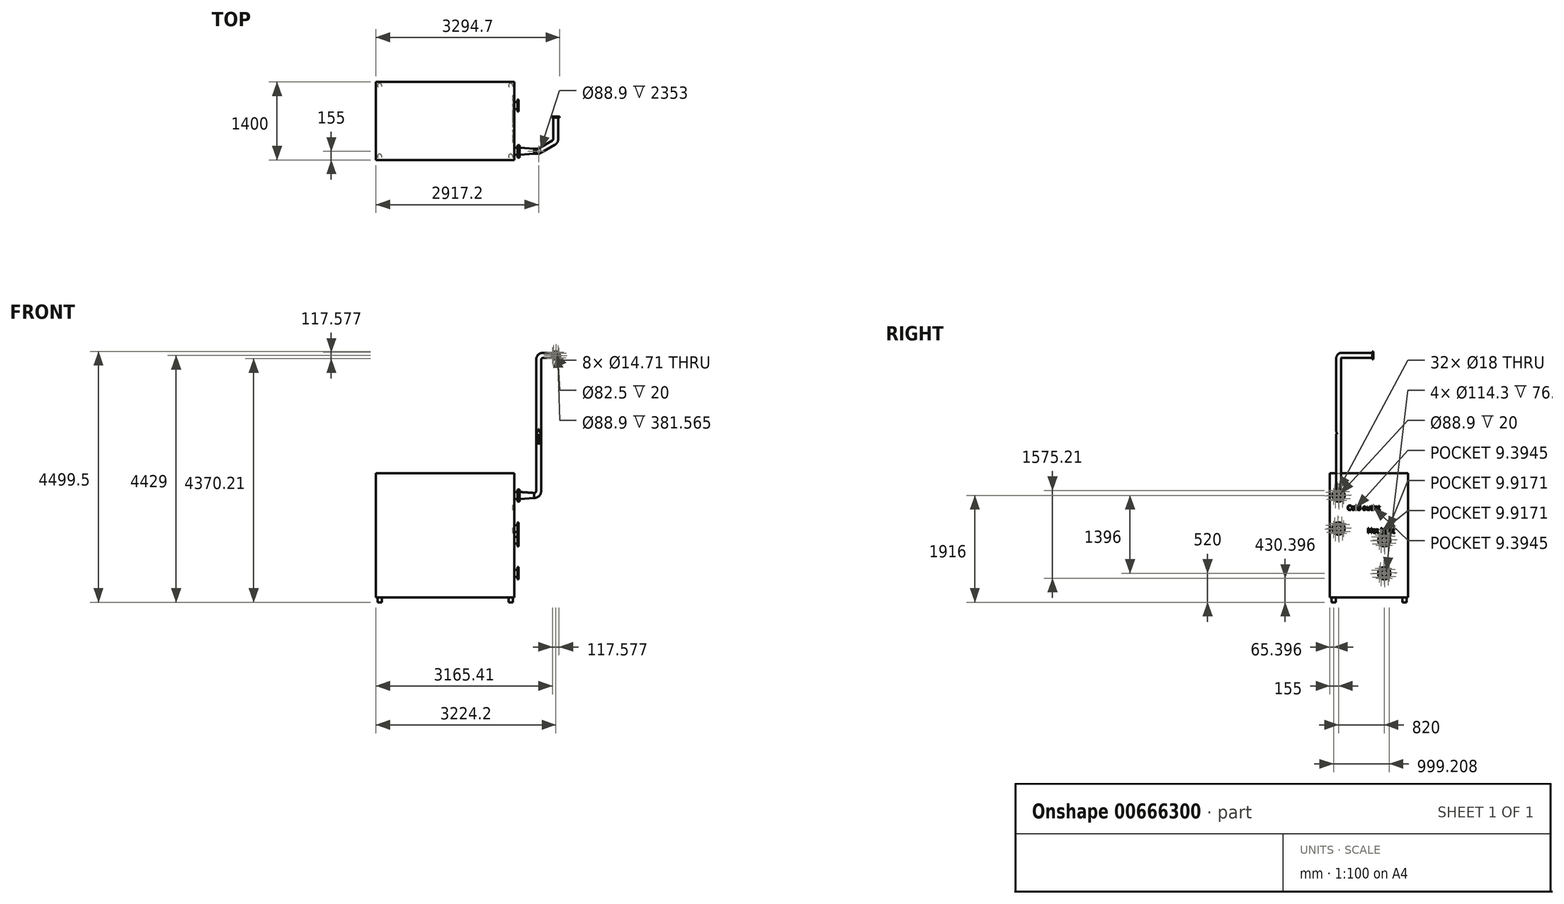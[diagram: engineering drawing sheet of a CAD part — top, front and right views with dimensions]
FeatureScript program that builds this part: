
annotation { "Feature Type Name" : "Feature", "Feature Type Description" : "" }
export const myFeature = defineFeature(function(context is Context, id is Id, definition is map)
    precondition{}
    {
        {
            var Q0;
            Q0=qCreatedBy(makeId("Top.planeOp"),FACE);
            var sketch = newSketch(context, id + "F0", { "sketchPlane" : qUnion([Q0])});
            skLineSegment(sketch, "E0.bottom", {"start": v(0, 0) * mm, "end": v(2481, 0) * mm});
            skLineSegment(sketch, "E0.top", {"start": v(0, 1400) * mm, "end": v(2481, 1400) * mm});
            skLineSegment(sketch, "E0.left", {"start": v(0, 0) * mm, "end": v(0, 1400) * mm});
            skLineSegment(sketch, "E0.right", {"start": v(2481, 0) * mm, "end": v(2481, 1400) * mm});
            skSolve(sketch);
        }
        {
            var Q0;
            Q0=qSketchRegion(id+"F0",true);
            extrude(context, id + "F1", {"entities" : qUnion([Q0]), "depth" : (2228 + 90) * mm});
        }
        {
            var Q0;
            Q0=makeQuery(id+"F1.opExtrude","SWEPT_FACE",FACE,{"disambiguationData":[OSD([sQuery(id+"F0.wireOp",EDGE,"E0.right")])]});
            var sketch = newSketch(context, id + "F2", { "sketchPlane" : qUnion([Q0])});
            skCircle(sketch, "E1", {"center": v(155, 1916) * mm, "radius": 57.15 * mm});
            skCircle(sketch, "E2", {"center": v(155, 1916) * mm, "radius": 62.15 * mm});
            skCircle(sketch, "E3", {"center": v(155, 1916) * mm, "radius": 110 * mm});
            skCircle(sketch, "E4", {"center": v(155, 1916) * mm, "radius": 90 * mm, "construction": true});
            skCircle(sketch, "E5", {"center": v(163.43, 1826.4) * mm, "radius": 9 * mm});
            skCircle(sketch, "E6.1.0", {"center": v(224.32, 1858.6) * mm, "radius": 9 * mm});
            skCircle(sketch, "E6.2.0", {"center": v(244.6, 1924.43) * mm, "radius": 9 * mm});
            skCircle(sketch, "E6.3.0", {"center": v(212.4, 1985.32) * mm, "radius": 9 * mm});
            skCircle(sketch, "E6.4.0", {"center": v(146.57, 2005.6) * mm, "radius": 9 * mm});
            skCircle(sketch, "E6.5.0", {"center": v(85.68, 1973.4) * mm, "radius": 9 * mm});
            skCircle(sketch, "E6.6.0", {"center": v(65.4, 1907.57) * mm, "radius": 9 * mm});
            skCircle(sketch, "E6.7.0", {"center": v(97.6, 1846.68) * mm, "radius": 9 * mm});
            skPoint(sketch, "E7.0.1.2", {"position": v(155, 1323) * mm});
            skCircle(sketch, "E7.0.1.4", {"center": v(155, 1323) * mm, "radius": 57.15 * mm});
            skCircle(sketch, "E7.0.1.5", {"center": v(155, 1323) * mm, "radius": 62.15 * mm});
            skCircle(sketch, "E7.0.1.6", {"center": v(155, 1323) * mm, "radius": 110 * mm});
            skCircle(sketch, "E7.0.1.7", {"center": v(155, 1323) * mm, "radius": 90 * mm, "construction": true});
            skCircle(sketch, "E7.0.1.13", {"center": v(97.6, 1253.68) * mm, "radius": 9 * mm});
            skCircle(sketch, "E7.0.1.15", {"center": v(244.6, 1331.43) * mm, "radius": 9 * mm});
            skCircle(sketch, "E7.0.1.16", {"center": v(212.4, 1392.32) * mm, "radius": 9 * mm});
            skCircle(sketch, "E7.0.1.17", {"center": v(146.57, 1412.6) * mm, "radius": 9 * mm});
            skCircle(sketch, "E7.0.1.18", {"center": v(163.43, 1233.4) * mm, "radius": 9 * mm});
            skCircle(sketch, "E7.0.1.19", {"center": v(85.68, 1380.4) * mm, "radius": 9 * mm});
            skCircle(sketch, "E7.0.1.20", {"center": v(65.4, 1314.57) * mm, "radius": 9 * mm});
            skCircle(sketch, "E7.0.1.21", {"center": v(224.32, 1265.6) * mm, "radius": 9 * mm});
            skLineSegment(sketch, "E7.direction1", {"start": v(97.6, 1846.68) * mm, "end": v(122.6, 1846.68) * mm, "construction": true});
            skLineSegment(sketch, "E7.direction2", {"start": v(97.6, 1846.68) * mm, "end": v(97.6, 1259.36) * mm, "construction": true});
            skSolve(sketch);
        }
        {
            var Q0;
            Q0=makeQuery(id+"F2.imprint","IMPRINT",FACE,{"disambiguationData":[TD([[makeQuery(id+"F2.imprint","IMPRINT",EDGE,{"derivedFrom":sQuery(id+"F2.wireOp",EDGE,"E1")}),-1.0]])]});
            var Q1;
            Q1=makeQuery(id+"F2.imprint","IMPRINT",FACE,{"disambiguationData":[TD([[makeQuery(id+"F2.imprint","IMPRINT",EDGE,{"derivedFrom":sQuery(id+"F2.wireOp",EDGE,"E7.0.1.4")}),-1.0]])]});
            extrude(context, id + "F3", {"entities" : qUnion([Q0, Q1]), "depth" : (76.2 - 22) * mm});
        }
        {
            var Q0;
            Q0=makeQuery(id+"F2.imprint","IMPRINT",FACE,{"disambiguationData":[TD([[makeQuery(id+"F2.imprint","IMPRINT",EDGE,{"derivedFrom":sQuery(id+"F2.wireOp",EDGE,"E7.0.1.4")}),-1.0]])]});
            var Q1;
            Q1=makeQuery(id+"F2.imprint","IMPRINT",FACE,{"disambiguationData":[TD([[makeQuery(id+"F2.imprint","IMPRINT",EDGE,{"derivedFrom":sQuery(id+"F2.wireOp",EDGE,"E7.0.1.5")}),-1.0]])]});
            var Q2;
            Q2=makeQuery(id+"F2.imprint","IMPRINT",FACE,{"disambiguationData":[TD([[makeQuery(id+"F2.imprint","IMPRINT",EDGE,{"derivedFrom":sQuery(id+"F2.wireOp",EDGE,"E1")}),-1.0]])]});
            var Q3;
            Q3=makeQuery(id+"F2.imprint","IMPRINT",FACE,{"disambiguationData":[TD([[makeQuery(id+"F2.imprint","IMPRINT",EDGE,{"derivedFrom":sQuery(id+"F2.wireOp",EDGE,"E2")}),-1.0]])]});
            var Q4;
            Q4=makeQuery(id+"F3.opExtrude","CAP_FACE",FACE,{"disambiguationData":[OSD([sQuery(id+"F2.wireOp",EDGE,"E7.0.1.4"),sQuery(id+"F2.wireOp",EDGE,"E7.0.1.5")])],"isStart":false});
            extrude(context, id + "F4", {"entities" : qUnion([Q0, Q1, Q2, Q3]), "operationType" : NewBodyOperationType.ADD, "depth" : 76.2 * mm, "hasSecondDirection" : true, "secondDirectionBound" : BoundingType.UP_TO_SURFACE, "secondDirectionOppositeDirection" : false, "secondDirectionBoundEntityFace" : qUnion([Q4]), "secondDirectionDepth" : 104.68 * mm});
        }
        {
            var Q0;
            Q0=makeQuery(id+"F3.opExtrude","SWEPT_BODY",BODY,{"disambiguationData":[OSD([sQuery(id+"F2.wireOp",EDGE,"E1"),sQuery(id+"F2.wireOp",EDGE,"E2")])]});
            var Q1;
            Q1=makeQuery(id+"F3.opExtrude","SWEPT_BODY",BODY,{"disambiguationData":[OSD([sQuery(id+"F2.wireOp",EDGE,"E7.0.1.4"),sQuery(id+"F2.wireOp",EDGE,"E7.0.1.5")])]});
            transform(context, id + "F5", {"entities" : qUnion([Q0, Q1]), "transformType" : TransformType.TRANSLATION_3D, "dx" : 0 * mm, "dy" : (975 - 155) * mm, "dz" : (430 - 1233) * mm, "makeCopy" : true});
        }
        {
            var Q0;
            Q0=makeQuery(id+"F1.opExtrude","SWEPT_BODY",BODY,{"disambiguationData":[OSD([sQuery(id+"F0.wireOp",EDGE,"E0.bottom"),sQuery(id+"F0.wireOp",EDGE,"E0.top"),sQuery(id+"F0.wireOp",EDGE,"E0.left"),sQuery(id+"F0.wireOp",EDGE,"E0.right")])]});
            var Q1;
            Q1=makeQuery(id+"F3.opExtrude","SWEPT_BODY",BODY,{"disambiguationData":[OSD([sQuery(id+"F2.wireOp",EDGE,"E1"),sQuery(id+"F2.wireOp",EDGE,"E2")])]});
            var Q2;
            Q2=makeQuery(id+"F3.opExtrude","SWEPT_BODY",BODY,{"disambiguationData":[OSD([sQuery(id+"F2.wireOp",EDGE,"E7.0.1.4"),sQuery(id+"F2.wireOp",EDGE,"E7.0.1.5")])]});
            var Q3;
            Q3=makeQuery(id+"F5.opPattern","COPY",BODY,{"derivedFrom":makeQuery(id+"F3.opExtrude","SWEPT_BODY",BODY,{"disambiguationData":[OSD([sQuery(id+"F2.wireOp",EDGE,"E7.0.1.4"),sQuery(id+"F2.wireOp",EDGE,"E7.0.1.5")])]}),"instanceName":"1"});
            var Q4;
            Q4=makeQuery(id+"F5.opPattern","COPY",BODY,{"derivedFrom":makeQuery(id+"F3.opExtrude","SWEPT_BODY",BODY,{"disambiguationData":[OSD([sQuery(id+"F2.wireOp",EDGE,"E1"),sQuery(id+"F2.wireOp",EDGE,"E2")])]}),"instanceName":"1"});
            booleanBodies(context, id + "F6", {"operationType" : BooleanOperationType.UNION, "tools" : qUnion([Q0, Q1, Q2, Q3, Q4])});
        }
        {
            var Q0;
            Q0=makeQuery(id+"F2.imprint","IMPRINT",FACE,{"disambiguationData":[TD([[makeQuery(id+"F2.imprint","IMPRINT",EDGE,{"derivedFrom":sQuery(id+"F2.wireOp",EDGE,"E3")}),-1.0]])]});
            var sketch = newSketch(context, id + "F7", { "sketchPlane" : qUnion([Q0])});
            skText(sketch, "E8", { "text": "Hot inlet", "fontName": "OpenSans-Regular.ttf"});
            skText(sketch, "E9", { "text": "Cold outlet\n", "fontName": "OpenSans-Regular.ttf"});
            const initialGuessF7  = {"E8": [0.67256, 1.24268, 1, 0, 0.08805], "E9": [0.3111, 1.65511, 1, 0, 0.08341]};
            skSetInitialGuess(sketch, initialGuessF7);
            skSolve(sketch);
        }
        {
            var Q0;
            Q0=qSketchRegion(id+"F7",true);
            extrude(context, id + "F8", {"entities" : qUnion([Q0]), "operationType" : NewBodyOperationType.REMOVE, "oppositeDirection" : true, "depth" : 25 * mm});
        }
        {
            var Q0;
            Q0=sQuery(id+"F2.wireOp",VERTEX,"E1.center");
            var Q1;
            Q1=qCreatedBy(makeId("Front.planeOp"),FACE);
            cPlane(context, id + "F9", {"entities" : qUnion([Q0, Q1]), "cplaneType" : CPlaneType.PLANE_POINT, "offset" : 150 * mm, "width" : 150 * mm, "height" : 150 * mm});
        }
        {
            var Q0;
            Q0=qCreatedBy(id+"F9.planeOp",FACE);
            var sketch = newSketch(context, id + "F10", { "sketchPlane" : qUnion([Q0])});
            skLineSegment(sketch, "E10.0", {"start": v(2557.2, 1973.15) * mm, "end": v(2557.2, 1858.85) * mm});
            skPoint(sketch, "E11", {"position": v(2557.2, 1916) * mm});
            skLineSegment(sketch, "E12", {"start": v(2557.2, 1916) * mm, "end": v(2837.2, 1916) * mm});
            skLineSegment(sketch, "E13", {"start": v(2917.2, 1996) * mm, "end": v(2917.2, 4349) * mm, "construction": true});
            skLineSegment(sketch, "E14", {"start": v(2997.2, 4429) * mm, "end": v(4002.78, 4429) * mm, "construction": true});
            skPoint(sketch, "E15.visualSharp", {"position": v(2917.2, 4429) * mm});
            skArc(sketch, "E15.filletArc", {"start": v(2997.2, 4429) * mm, "mid": v(2940.63, 4405.57) * mm, "end": v(2917.2, 4349) * mm, "construction": true});
            skPoint(sketch, "E16.visualSharp", {"position": v(2917.2, 1916) * mm});
            skArc(sketch, "E16.filletArc", {"start": v(2837.2, 1916) * mm, "mid": v(2893.77, 1939.43) * mm, "end": v(2917.2, 1996) * mm});
            skLineSegment(sketch, "E17", {"start": v(2917.2, 2846.37) * mm, "end": v(2898.2, 2846.37) * mm});
            skLineSegment(sketch, "E18", {"start": v(2898.2, 2846.37) * mm, "end": v(2898.2, 3020.37) * mm});
            skLineSegment(sketch, "E19", {"start": v(2898.2, 3020.37) * mm, "end": v(2878.2, 3020.37) * mm});
            skLineSegment(sketch, "E20", {"start": v(2878.2, 3020.37) * mm, "end": v(2917.2, 3112.37) * mm});
            skLineSegment(sketch, "E21.MirrorCS", {"start": v(2956.2, 3020.37) * mm, "end": v(2917.2, 3112.37) * mm});
            skLineSegment(sketch, "E22.MirrorCS", {"start": v(2936.2, 2846.37) * mm, "end": v(2936.2, 3020.37) * mm});
            skLineSegment(sketch, "E23.MirrorCS", {"start": v(2936.2, 3020.37) * mm, "end": v(2956.2, 3020.37) * mm});
            skLineSegment(sketch, "E24.MirrorCS", {"start": v(2917.2, 2846.37) * mm, "end": v(2936.2, 2846.37) * mm});
            skLineSegment(sketch, "E25", {"start": v(2917.2, 1996) * mm, "end": v(2917.2, 2492.37) * mm});
            skSolve(sketch);
        }
        {
            var Q0;
            Q0=sQuery(id+"F10.wireOp",VERTEX,"E14.end");
            var Q1;
            Q1=qCreatedBy(makeId("Top.planeOp"),FACE);
            cPlane(context, id + "F11", {"entities" : qUnion([Q0, Q1]), "cplaneType" : CPlaneType.PLANE_POINT, "offset" : 150 * mm, "width" : 150 * mm, "height" : 150 * mm});
        }
        {
            var Q0;
            Q0=makeQuery(id+"F4.opExtrude","CAP_FACE",FACE,{"disambiguationData":[OSD([sQuery(id+"F2.wireOp",EDGE,"E1"),sQuery(id+"F2.wireOp",EDGE,"E3"),sQuery(id+"F2.wireOp",EDGE,"E5"),sQuery(id+"F2.wireOp",EDGE,"E6.1.0"),sQuery(id+"F2.wireOp",EDGE,"E6.2.0"),sQuery(id+"F2.wireOp",EDGE,"E6.3.0"),sQuery(id+"F2.wireOp",EDGE,"E6.4.0"),sQuery(id+"F2.wireOp",EDGE,"E6.5.0"),sQuery(id+"F2.wireOp",EDGE,"E6.6.0"),sQuery(id+"F2.wireOp",EDGE,"E6.7.0")])],"isStart":false});
            var sketch = newSketch(context, id + "F12", { "sketchPlane" : qUnion([Q0])});
            skCircle(sketch, "E26", {"center": v(155, 1916) * mm, "radius": 45.25 * mm});
            skCircle(sketch, "E27", {"center": v(155, 1916) * mm, "radius": 44.45 * mm});
            skCircle(sketch, "E28.0", {"center": v(155, 1916) * mm, "radius": 110 * mm});
            skCircle(sketch, "E28.1", {"center": v(85.68, 1973.4) * mm, "radius": 9 * mm});
            skCircle(sketch, "E28.2", {"center": v(65.4, 1907.57) * mm, "radius": 9 * mm});
            skCircle(sketch, "E28.3", {"center": v(97.6, 1846.68) * mm, "radius": 9 * mm});
            skCircle(sketch, "E28.4", {"center": v(163.43, 1826.4) * mm, "radius": 9 * mm});
            skCircle(sketch, "E28.5", {"center": v(224.32, 1858.6) * mm, "radius": 9 * mm});
            skCircle(sketch, "E28.6", {"center": v(244.6, 1924.43) * mm, "radius": 9 * mm});
            skCircle(sketch, "E28.7", {"center": v(212.4, 1985.32) * mm, "radius": 9 * mm});
            skCircle(sketch, "E28.8", {"center": v(146.57, 2005.6) * mm, "radius": 9 * mm});
            skSolve(sketch);
        }
        {
            var Q0;
            Q0=qCreatedBy(id+"F11.planeOp",FACE);
            var sketch = newSketch(context, id + "F13", { "sketchPlane" : qUnion([Q0])});
            skPoint(sketch, "E29.0", {"position": v(4002.78, 155) * mm});
            skLineSegment(sketch, "E30", {"start": v(4002.78, 155) * mm, "end": v(4016.77, 155) * mm, "construction": true});
            skLineSegment(sketch, "E31", {"start": v(4662.92, 835.27) * mm, "end": v(4662.92, 928.63) * mm, "construction": true});
            skPoint(sketch, "E32.visualSharp", {"position": v(4662.92, 155) * mm});
            skPoint(sketch, "E33.0", {"position": v(2917.2, 155) * mm});
            skLineSegment(sketch, "E34", {"start": v(3478.84, 355.73) * mm, "end": v(4609.84, 759.93) * mm, "construction": true});
            skArc(sketch, "E35.filletArc", {"start": v(4609.84, 759.93) * mm, "mid": v(4648.31, 789.2) * mm, "end": v(4662.92, 835.27) * mm, "construction": true});
            skPoint(sketch, "E36", {"position": v(3478.84, 355.73) * mm});
            skSolve(sketch);
        }
        {
            var Q0;
            Q0=sQuery(id+"F10.wireOp",VERTEX,"E15.visualSharp");
            var Q1;
            Q1=sQuery(id+"F10.wireOp",VERTEX,"E15.filletArc.end");
            var Q2;
            Q2=sQuery(id+"F13.wireOp",VERTEX,"E36");
            cPlane(context, id + "F14", {"entities" : qUnion([Q0, Q1, Q2]), "cplaneType" : CPlaneType.THREE_POINT, "offset" : 150 * mm, "width" : 150 * mm, "height" : 150 * mm});
        }
        {
            var Q0;
            Q0=sQuery(id+"F10.wireOp",EDGE,"E12");
            var Q1;
            Q1=sQuery(id+"F10.wireOp",VERTEX,"E16.visualSharp");
            cPlane(context, id + "F15", {"entities" : qUnion([Q0, Q1]), "cplaneType" : CPlaneType.LINE_POINT, "offset" : 150 * mm, "width" : 150 * mm, "height" : 150 * mm});
        }
        {
            var Q0;
            Q0=qCreatedBy(id+"F15.planeOp",FACE);
            var sketch = newSketch(context, id + "F16", { "sketchPlane" : qUnion([Q0])});
            skLineSegment(sketch, "E37.0", {"start": v(155, 2492.37) * mm, "end": v(155, 4349) * mm});
            skLineSegment(sketch, "E38", {"start": v(155, 4349) * mm, "end": v(155, 4349) * mm});
            skLineSegment(sketch, "E39", {"start": v(235, 4429) * mm, "end": v(252.39, 4429) * mm, "construction": true});
            skPoint(sketch, "E40.visualSharp", {"position": v(155, 4429) * mm});
            skArc(sketch, "E40.filletArc", {"start": v(235, 4429) * mm, "mid": v(178.43, 4405.57) * mm, "end": v(155, 4349) * mm, "construction": true});
            skPoint(sketch, "E41.0", {"position": v(155, 2492.37) * mm});
            skPoint(sketch, "E42.orphan", {"position": v(155, 1996) * mm});
            skSolve(sketch);
        }
        {
            var Q0;
            Q0=sQuery(id+"F16.wireOp",EDGE,"E37.0");
            cPlane(context, id + "F17", {"entities" : qUnion([Q0]), "cplaneType" : CPlaneType.LINE_ANGLE, "offset" : 150 * mm, "angle" : 120 * degree, "width" : 150 * mm, "height" : 150 * mm});
        }
        {
            var Q0;
            Q0=qCreatedBy(id+"F17.planeOp",FACE);
            var sketch = newSketch(context, id + "F18", { "sketchPlane" : qUnion([Q0])});
            skPoint(sketch, "E43.0", {"position": v(-2603.87, 4429) * mm});
            skLineSegment(sketch, "E44.0", {"start": v(-2603.87, 2492.37) * mm, "end": v(-2603.87, 4349) * mm});
            skLineSegment(sketch, "E45", {"start": v(-2603.87, 4349) * mm, "end": v(-2603.87, 4349) * mm});
            skLineSegment(sketch, "E46", {"start": v(-2683.87, 4429) * mm, "end": v(-2686.37, 4429) * mm});
            skArc(sketch, "E47.filletArc", {"start": v(-2603.87, 4349) * mm, "mid": v(-2627.3, 4405.57) * mm, "end": v(-2683.87, 4429) * mm});
            skSolve(sketch);
        }
        {
            var Q0;
            Q0=qCreatedBy(id+"F11.planeOp",FACE);
            var sketch = newSketch(context, id + "F19", { "sketchPlane" : qUnion([Q0])});
            skPoint(sketch, "E48.0", {"position": v(2917.2, 252.39) * mm});
            skLineSegment(sketch, "E49", {"start": v(2917.2, 252.39) * mm, "end": v(2917.2, 447) * mm, "construction": true});
            skLineSegment(sketch, "E50", {"start": v(2997.2, 527) * mm, "end": v(3144.2, 527) * mm, "construction": true});
            skLineSegment(sketch, "E51", {"start": v(3224.2, 607) * mm, "end": v(3224.2, 780) * mm});
            skPoint(sketch, "E52.visualSharp", {"position": v(2917.2, 527) * mm});
            skArc(sketch, "E52.filletArc", {"start": v(2997.2, 527) * mm, "mid": v(2940.63, 503.57) * mm, "end": v(2917.2, 447) * mm, "construction": true});
            skPoint(sketch, "E53.visualSharp", {"position": v(3224.2, 527) * mm});
            skArc(sketch, "E53.filletArc", {"start": v(3144.2, 527) * mm, "mid": v(3200.77, 550.43) * mm, "end": v(3224.2, 607) * mm, "construction": true});
            skPoint(sketch, "E54.0", {"position": v(2988.64, 196.25) * mm});
            skLineSegment(sketch, "E55", {"start": v(2988.64, 196.25) * mm, "end": v(3184.2, 309.15) * mm});
            skLineSegment(sketch, "E56", {"start": v(3224.2, 378.43) * mm, "end": v(3224.2, 607) * mm});
            skPoint(sketch, "E57.visualSharp", {"position": v(3224.2, 332.25) * mm});
            skArc(sketch, "E57.filletArc", {"start": v(3184.2, 309.15) * mm, "mid": v(3213.48, 338.43) * mm, "end": v(3224.2, 378.43) * mm});
            skSolve(sketch);
        }
        {
            var Q0;
            Q0=makeQuery(id+"F12.imprint","IMPRINT",FACE,{"disambiguationData":[TD([[makeQuery(id+"F12.imprint","IMPRINT",EDGE,{"derivedFrom":sQuery(id+"F12.wireOp",EDGE,"E26")}),1.0]])]});
            var Q1;
            Q1=sQuery(id+"F10.wireOp",EDGE,"E12");
            var Q2;
            Q2=sQuery(id+"F10.wireOp",EDGE,"E16.filletArc");
            var Q3;
            Q3=sQuery(id+"F10.wireOp",EDGE,"E25");
            var Q4;
            Q4=sQuery(id+"F16.wireOp",EDGE,"E37.0");
            var Q5;
            Q5=sQuery(id+"F16.wireOp",EDGE,"E40.filletArc");
            var Q6;
            Q6=sQuery(id+"F16.wireOp",EDGE,"E39");
            var Q7;
            Q7=sQuery(id+"F18.wireOp",EDGE,"E47.filletArc");
            var Q8;
            Q8=sQuery(id+"F18.wireOp",EDGE,"E46");
            var Q9;
            Q9=sQuery(id+"F19.wireOp",EDGE,"E55");
            var Q10;
            Q10=sQuery(id+"F19.wireOp",EDGE,"E57.filletArc");
            var Q11;
            Q11=sQuery(id+"F19.wireOp",EDGE,"E56");
            var Q12;
            Q12=sQuery(id+"F19.wireOp",EDGE,"E51");
            sweep(context, id + "F20", {"profiles" : qUnion([Q0]), "path" : qUnion([Q1, Q2, Q3, Q4, Q5, Q6, Q7, Q8, Q9, Q10, Q11, Q12])});
        }
        {
            var Q0;
            Q0=makeQuery(id+"F10.imprint","IMPRINT",FACE,{"disambiguationData":[TD([[makeQuery(id+"F10.imprint","IMPRINT",EDGE,{"derivedFrom":sQuery(id+"F10.wireOp",EDGE,"E17")}),-1.0]])]});
            var Q1;
            Q1=makeQuery(id+"F20.opSweep","SWEPT_FACE",FACE,{"disambiguationData":[OSD([sQuery(id+"F10.wireOp",EDGE,"E25"),sQuery(id+"F12.wireOp",EDGE,"E26")])]});
            extrude(context, id + "F21", {"entities" : qUnion([Q0]), "operationType" : NewBodyOperationType.REMOVE, "endBound" : BoundingType.UP_TO_SURFACE, "endBoundEntityFace" : qUnion([Q1]), "depth" : 25 * mm});
        }
        {
            var Q0;
            Q0=makeQuery(id+"F12.imprint","IMPRINT",FACE,{"disambiguationData":[TD([[makeQuery(id+"F12.imprint","IMPRINT",EDGE,{"derivedFrom":sQuery(id+"F12.wireOp",EDGE,"5eb4fbdf-50e4-4599-8a57-953bda03fb07")}),1.0]])]});
            var Q1;
            {var subQ0=makeQuery(id+"F4.opExtrude","CAP_EDGE",EDGE,{"disambiguationData":[OSD([sQuery(id+"F2.wireOp",EDGE,"E6.5.0")])],"isStart":false});var subQ1=sQuery(id+"F12.wireOp",EDGE,"10598bff-0ce2-465f-aa84-94724ede3573.5.0");var subQ3=makeQuery(id+"F12.imprint","INTERSECT",VERTEX,{"disambiguationData":[OD(0.0)],"derivedFrom":[subQ0,subQ1]});Q1=makeQuery(id+"F12.imprint","IMPRINT",FACE,{"disambiguationData":[TD([[makeQuery(id+"F12.imprint","IMPRINT",EDGE,{"disambiguationData":[TD([[subQ3,1.0]])],"derivedFrom":subQ1}),-1.0]])]});}
            var Q2;
            {var subQ0=makeQuery(id+"F4.opExtrude","CAP_EDGE",EDGE,{"disambiguationData":[OSD([sQuery(id+"F2.wireOp",EDGE,"E6.6.0")])],"isStart":false});var subQ1=sQuery(id+"F12.wireOp",EDGE,"10598bff-0ce2-465f-aa84-94724ede3573.6.0");var subQ3=makeQuery(id+"F12.imprint","INTERSECT",VERTEX,{"disambiguationData":[OD(0.0)],"derivedFrom":[subQ0,subQ1]});Q2=makeQuery(id+"F12.imprint","IMPRINT",FACE,{"disambiguationData":[TD([[makeQuery(id+"F12.imprint","IMPRINT",EDGE,{"disambiguationData":[TD([[subQ3,1.0]])],"derivedFrom":subQ1}),-1.0]])]});}
            var Q3;
            {var subQ0=makeQuery(id+"F4.opExtrude","CAP_EDGE",EDGE,{"disambiguationData":[OSD([sQuery(id+"F2.wireOp",EDGE,"E6.7.0")])],"isStart":false});var subQ1=sQuery(id+"F12.wireOp",EDGE,"10598bff-0ce2-465f-aa84-94724ede3573.7.0");var subQ3=makeQuery(id+"F12.imprint","INTERSECT",VERTEX,{"disambiguationData":[OD(0.0)],"derivedFrom":[subQ0,subQ1]});Q3=makeQuery(id+"F12.imprint","IMPRINT",FACE,{"disambiguationData":[TD([[makeQuery(id+"F12.imprint","IMPRINT",EDGE,{"disambiguationData":[TD([[subQ3,-1.0]])],"derivedFrom":subQ1}),-1.0]])]});}
            var Q4;
            {var subQ0=makeQuery(id+"F4.opExtrude","CAP_EDGE",EDGE,{"disambiguationData":[OSD([sQuery(id+"F2.wireOp",EDGE,"E5")])],"isStart":false});var subQ1=sQuery(id+"F12.wireOp",EDGE,"f2602a40-a317-41e3-a5e0-55ea5d988d8e");var subQ3=makeQuery(id+"F12.imprint","INTERSECT",VERTEX,{"disambiguationData":[OD(0.0)],"derivedFrom":[subQ0,subQ1]});Q4=makeQuery(id+"F12.imprint","IMPRINT",FACE,{"disambiguationData":[TD([[makeQuery(id+"F12.imprint","IMPRINT",EDGE,{"disambiguationData":[TD([[subQ3,-1.0]])],"derivedFrom":subQ1}),-1.0]])]});}
            var Q5;
            {var subQ0=makeQuery(id+"F4.opExtrude","CAP_EDGE",EDGE,{"disambiguationData":[OSD([sQuery(id+"F2.wireOp",EDGE,"E6.1.0")])],"isStart":false});var subQ1=sQuery(id+"F12.wireOp",EDGE,"10598bff-0ce2-465f-aa84-94724ede3573.1.0");var subQ3=makeQuery(id+"F12.imprint","INTERSECT",VERTEX,{"disambiguationData":[OD(0.0)],"derivedFrom":[subQ0,subQ1]});Q5=makeQuery(id+"F12.imprint","IMPRINT",FACE,{"disambiguationData":[TD([[makeQuery(id+"F12.imprint","IMPRINT",EDGE,{"disambiguationData":[TD([[subQ3,-1.0]])],"derivedFrom":subQ1}),-1.0]])]});}
            var Q6;
            {var subQ0=makeQuery(id+"F4.opExtrude","CAP_EDGE",EDGE,{"disambiguationData":[OSD([sQuery(id+"F2.wireOp",EDGE,"E6.3.0")])],"isStart":false});var subQ1=sQuery(id+"F12.wireOp",EDGE,"10598bff-0ce2-465f-aa84-94724ede3573.3.0");var subQ3=makeQuery(id+"F12.imprint","INTERSECT",VERTEX,{"disambiguationData":[OD(0.0)],"derivedFrom":[subQ0,subQ1]});Q6=makeQuery(id+"F12.imprint","IMPRINT",FACE,{"disambiguationData":[TD([[makeQuery(id+"F12.imprint","IMPRINT",EDGE,{"disambiguationData":[TD([[subQ3,1.0]])],"derivedFrom":subQ1}),-1.0]])]});}
            var Q7;
            {var subQ0=makeQuery(id+"F4.opExtrude","CAP_EDGE",EDGE,{"disambiguationData":[OSD([sQuery(id+"F2.wireOp",EDGE,"E6.4.0")])],"isStart":false});var subQ1=sQuery(id+"F12.wireOp",EDGE,"10598bff-0ce2-465f-aa84-94724ede3573.4.0");var subQ3=makeQuery(id+"F12.imprint","INTERSECT",VERTEX,{"disambiguationData":[OD(0.0)],"derivedFrom":[subQ0,subQ1]});Q7=makeQuery(id+"F12.imprint","IMPRINT",FACE,{"disambiguationData":[TD([[makeQuery(id+"F12.imprint","IMPRINT",EDGE,{"disambiguationData":[TD([[subQ3,1.0]])],"derivedFrom":subQ1}),-1.0]])]});}
            var Q8;
            {var subQ0=makeQuery(id+"F4.opExtrude","CAP_EDGE",EDGE,{"disambiguationData":[OSD([sQuery(id+"F2.wireOp",EDGE,"E6.2.0")])],"isStart":false});var subQ1=sQuery(id+"F12.wireOp",EDGE,"10598bff-0ce2-465f-aa84-94724ede3573.2.0");var subQ3=makeQuery(id+"F12.imprint","INTERSECT",VERTEX,{"disambiguationData":[OD(0.0)],"derivedFrom":[subQ0,subQ1]});Q8=makeQuery(id+"F12.imprint","IMPRINT",FACE,{"disambiguationData":[TD([[makeQuery(id+"F12.imprint","IMPRINT",EDGE,{"disambiguationData":[TD([[subQ3,-1.0]])],"derivedFrom":subQ1}),-1.0]])]});}
            var Q9;
            Q9=makeQuery(id+"F12.imprint","IMPRINT",FACE,{"disambiguationData":[TD([[makeQuery(id+"F12.imprint","IMPRINT",EDGE,{"derivedFrom":sQuery(id+"F12.wireOp",EDGE,"E26")}),-1.0]])]});
            var Q10;
            Q10=makeQuery(id+"F12.imprint","IMPRINT",FACE,{"disambiguationData":[TD([[makeQuery(id+"F12.imprint","IMPRINT",EDGE,{"derivedFrom":sQuery(id+"F12.wireOp",EDGE,"E28.0")}),1.0]])]});
            extrude(context, id + "F22", {"entities" : qUnion([Q0, Q1, Q2, Q3, Q4, Q5, Q6, Q7, Q8, Q9, Q10]), "operationType" : NewBodyOperationType.ADD, "depth" : 20 * mm});
        }
        {
            var Q0;
            Q0=makeQuery(id+"F20.opSweep","CAP_FACE",FACE,{"disambiguationData":[OSD([sQuery(id+"F12.wireOp",EDGE,"E26"),sQuery(id+"F12.wireOp",EDGE,"E27"),sQuery(id+"F13.wireOp",VERTEX,"E31.end")])],"isStart":false});
            var sketch = newSketch(context, id + "F23", { "sketchPlane" : qUnion([Q0])});
            skCircle(sketch, "E58", {"center": v(-3224.2, 4429) * mm, "radius": 70.5 * mm});
            skCircle(sketch, "E59.7.0", {"center": v(-3219.2, 4370.21) * mm, "radius": 7.35 * mm});
            skCircle(sketch, "E60", {"center": v(-3224.2, 4429) * mm, "radius": 59 * mm, "construction": true});
            skCircle(sketch, "E59.6.0", {"center": v(-3179.1, 4390.96) * mm, "radius": 7.35 * mm});
            skLineSegment(sketch, "E59.anchor2", {"start": v(-3224.2, 4429) * mm, "end": v(-3219.2, 4370.21) * mm, "construction": true});
            skCircle(sketch, "E61", {"center": v(-3224.2, 4429) * mm, "radius": 41.25 * mm});
            skCircle(sketch, "E62", {"center": v(-3262.24, 4383.9) * mm, "radius": 7.35 * mm});
            skLineSegment(sketch, "E59.anchor1", {"start": v(-3224.2, 4429) * mm, "end": v(-3262.24, 4383.9) * mm, "construction": true});
            skCircle(sketch, "E59.5.0", {"center": v(-3165.41, 4434) * mm, "radius": 7.35 * mm});
            skCircle(sketch, "E59.1.0", {"center": v(-3282.99, 4424) * mm, "radius": 7.35 * mm});
            skCircle(sketch, "E59.4.0", {"center": v(-3186.16, 4474.1) * mm, "radius": 7.35 * mm});
            skCircle(sketch, "E59.2.0", {"center": v(-3269.3, 4467.04) * mm, "radius": 7.35 * mm});
            skCircle(sketch, "E59.3.0", {"center": v(-3229.2, 4487.79) * mm, "radius": 7.35 * mm});
            skSolve(sketch);
        }
        {
            var Q0;
            Q0=qSketchRegion(id+"F23",true);
            extrude(context, id + "F24", {"entities" : qUnion([Q0]), "operationType" : NewBodyOperationType.ADD, "oppositeDirection" : true, "depth" : 20 * mm});
        }
        {
            var Q0;
            Q0=sQuery(id+"F10.wireOp",EDGE,"E12");
            cPlane(context, id + "F25", {"entities" : qUnion([Q0]), "cplaneType" : CPlaneType.LINE_ANGLE, "offset" : 150 * mm, "angle" : 0 * degree, "width" : 150 * mm, "height" : 150 * mm});
        }
        {
            var Q0;
            Q0=makeQuery(id+"F1.opExtrude","CAP_FACE",FACE,{"disambiguationData":[OSD([sQuery(id+"F0.wireOp",EDGE,"E0.bottom"),sQuery(id+"F0.wireOp",EDGE,"E0.top"),sQuery(id+"F0.wireOp",EDGE,"E0.left"),sQuery(id+"F0.wireOp",EDGE,"E0.right")])],"isStart":true});
            var sketch = newSketch(context, id + "F26", { "sketchPlane" : qUnion([Q0])});
            skLineSegment(sketch, "E63", {"start": v(0, -700) * mm, "end": v(2481, -700) * mm, "construction": true});
            skLineSegment(sketch, "E64", {"start": v(1240.5, 0) * mm, "end": v(1240.5, -1400) * mm, "construction": true});
            skCircle(sketch, "E65", {"center": v(65.58, -65.07) * mm, "radius": 38.33 * mm});
            skCircle(sketch, "E66.MirrorC", {"center": v(2415.42, -65.07) * mm, "radius": 38.33 * mm});
            skCircle(sketch, "E67.MirrorC", {"center": v(65.58, -1334.93) * mm, "radius": 38.33 * mm});
            skCircle(sketch, "E68.MirrorC", {"center": v(2415.42, -1334.93) * mm, "radius": 38.33 * mm});
            skLineSegment(sketch, "E69.0", {"start": v(0, 0) * mm, "end": v(2481, 0) * mm});
            skLineSegment(sketch, "E69.1", {"start": v(0, 0) * mm, "end": v(0, -1400) * mm});
            skLineSegment(sketch, "E69.2", {"start": v(0, -1400) * mm, "end": v(2481, -1400) * mm});
            skPoint(sketch, "E69.3", {"position": v(2481, -866.86) * mm});
            skLineSegment(sketch, "E69.4", {"start": v(2481, 0) * mm, "end": v(2481, -1400) * mm});
            skSolve(sketch);
        }
        {
            var Q0;
            Q0=qSketchRegion(id+"F26",true);
            extrude(context, id + "F27", {"entities" : qUnion([Q0]), "operationType" : NewBodyOperationType.REMOVE, "oppositeDirection" : true, "depth" : 90 * mm});
        }
        {
            var Q0;
            Q0=qCreatedBy(id+"F25.planeOp",FACE);
            var sketch = newSketch(context, id + "F28", { "sketchPlane" : qUnion([Q0])});
            skLineSegment(sketch, "E70.0", {"start": v(-2557.2, 1916) * mm, "end": v(-2837.2, 1916) * mm});
            skLineSegment(sketch, "E71.1", {"start": v(-2577.2, 1806) * mm, "end": v(-2577.2, 2026) * mm});
            skPoint(sketch, "E72", {"position": v(-2577.2, 1979.38) * mm});
            skLineSegment(sketch, "E73.0", {"start": v(-2837.2, 1870.75) * mm, "end": v(-2837.2, 1961.25) * mm});
            skLineSegment(sketch, "E74", {"start": v(-2837.2, 1961.25) * mm, "end": v(-2577.2, 1979.38) * mm});
            skSolve(sketch);
        }
        {
            var Q0;
            Q0=qSketchRegion(id+"F28",true);
            var Q1;
            Q1=sQuery(id+"F28.wireOp",EDGE,"E70.0");
            revolve(context, id + "F29", {"operationType" : NewBodyOperationType.ADD, "entities" : qUnion([Q0]), "axis" : qUnion([Q1]), "revolveType" : RevolveType.FULL});
        }
    });
